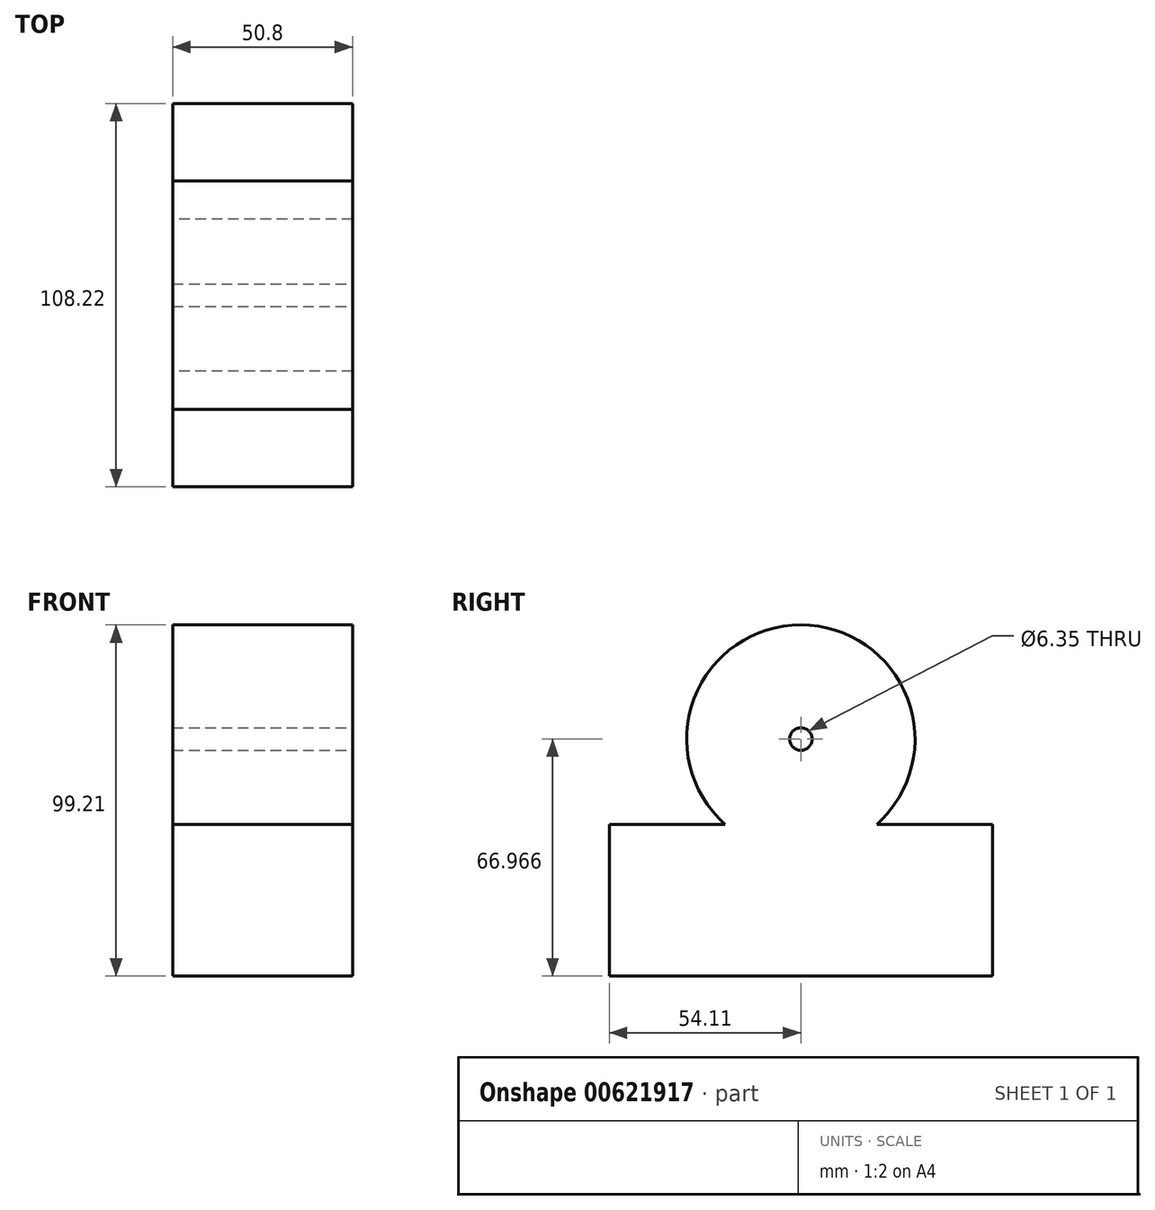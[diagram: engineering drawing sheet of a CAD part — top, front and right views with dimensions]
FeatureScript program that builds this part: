
annotation { "Feature Type Name" : "Feature", "Feature Type Description" : "" }
export const myFeature = defineFeature(function(context is Context, id is Id, definition is map)
    precondition{}
    {
        {
            var Q0;
            Q0=qCreatedBy(makeId("Right.planeOp"),FACE);
            var sketch = newSketch(context, id + "F0", { "sketchPlane" : qUnion([Q0])});
            skLineSegment(sketch, "E0.bottom", {"start": v(-54.1, -21.45) * mm, "end": v(54.1, -21.45) * mm});
            skLineSegment(sketch, "E0.top", {"start": v(-54.1, 21.45) * mm, "end": v(54.1, 21.45) * mm});
            skLineSegment(sketch, "E0.left", {"start": v(-54.1, -21.45) * mm, "end": v(-54.1, 21.45) * mm});
            skLineSegment(sketch, "E0.right", {"start": v(54.1, -21.45) * mm, "end": v(54.1, 21.45) * mm});
            skPoint(sketch, "E0.middle", {"position": v(0, 0) * mm});
            skCircle(sketch, "E1", {"center": v(0, 45.52) * mm, "radius": 32.25 * mm});
            skPoint(sketch, "E1.centerSnap0", {"position": v(0, 21.45) * mm});
            skPoint(sketch, "E2", {"position": v(-135.92, 13.35) * mm});
            skSolve(sketch);
        }
        {
            var Q0;
            {var subQ0=sQuery(id+"F0.wireOp",EDGE,"E0.bottom");Q0=makeQuery(id+"F0.imprint","IMPRINT",FACE,{"disambiguationData":[TD([[makeQuery(id+"F0.imprint","IMPRINT",EDGE,{"derivedFrom":subQ0}),1.0]])]});}
            extrude(context, id + "F1", {"entities" : qUnion([Q0]), "endBound" : BoundingType.SYMMETRIC, "depth" : 25.4 * mm, "offsetDistance" : 25.4 * mm});
        }
        {
            var Q0;
            Q0 = qSketchRegion(id + "F0", true);
            extrude(context, id + "F2", {"entities" : qUnion([Q0]), "operationType" : NewBodyOperationType.ADD, "endBound" : BoundingType.SYMMETRIC, "depth" : 50.8 * mm, "offsetDistance" : 25.4 * mm});
        }
        {
            var Q0;
            Q0=makeQuery(id+"F2.opExtrude","CAP_FACE",FACE,{"disambiguationData":[OSD([sQuery(id+"F0.wireOp",EDGE,"E0.bottom"),sQuery(id+"F0.wireOp",EDGE,"E0.top"),sQuery(id+"F0.wireOp",EDGE,"E0.left"),sQuery(id+"F0.wireOp",EDGE,"E0.right"),sQuery(id+"F0.wireOp",EDGE,"E1")])],"isStart":false});
            var sketch = newSketch(context, id + "F3", { "sketchPlane" : qUnion([Q0])});
            skPoint(sketch, "E3", {"position": v(0, 45.52) * mm});
            skSolve(sketch);
        }
        {
            var Q0;
            Q0=sQuery(id+"F3.wireOp",VERTEX,"E3");
            var Q1;
            Q1=makeQuery(id+"F1.opExtrude","SWEPT_BODY",BODY,{"disambiguationData":[OSD([sQuery(id+"F0.wireOp",EDGE,"E0.bottom"),sQuery(id+"F0.wireOp",EDGE,"E0.top"),sQuery(id+"F0.wireOp",EDGE,"E0.left"),sQuery(id+"F0.wireOp",EDGE,"E0.right"),sQuery(id+"F0.wireOp",EDGE,"E1")])]});
            hole(context, id + "F4", {"style" : HoleStyle.SIMPLE, "endStyle" : HoleEndStyle.THROUGH, "holeDiameter" : 6.35 * mm, "majorDiameter" : 6.35 * mm, "isTappedThrough" : true, "tappedDepth" : 12.7 * mm, "tapClearance" : 3, "locations" : qUnion([Q0]), "scope" : qUnion([Q1])});
        }
    });
